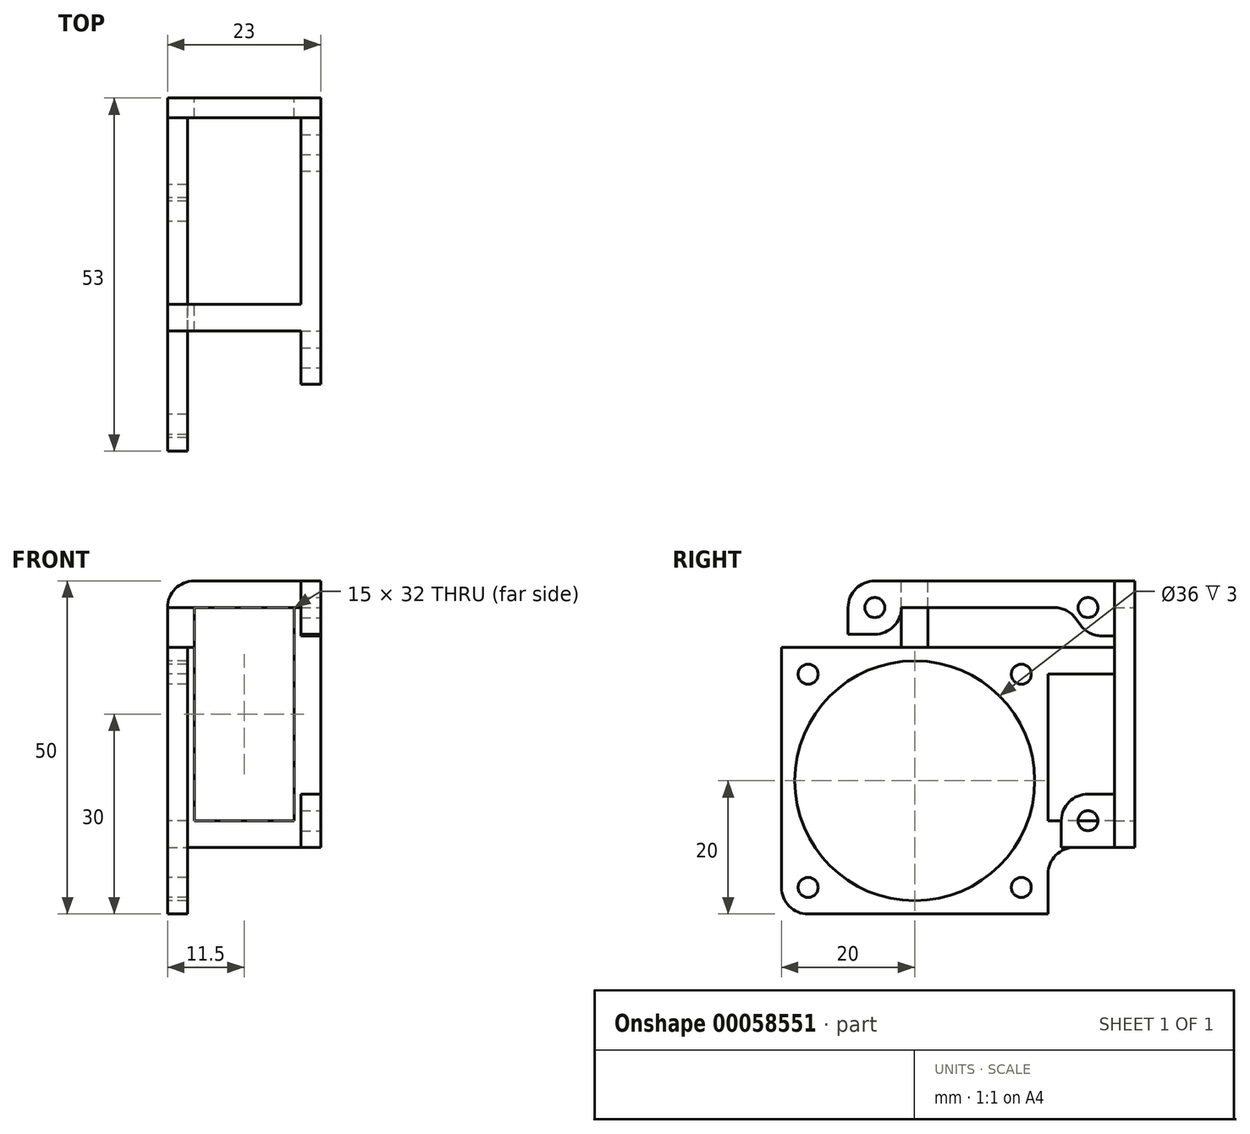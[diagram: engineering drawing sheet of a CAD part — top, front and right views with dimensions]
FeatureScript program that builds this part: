
annotation { "Feature Type Name" : "Feature", "Feature Type Description" : "" }
export const myFeature = defineFeature(function(context is Context, id is Id, definition is map)
    precondition{}
    {
        {
            var Q0;
            Q0=qCreatedBy(makeId("Top.planeOp"),FACE);
            var sketch = newSketch(context, id + "F0", { "sketchPlane" : qUnion([Q0])});
            skLineSegment(sketch, "E0.bottom", {"start": v(0, 0) * mm, "end": v(3, 0) * mm});
            skLineSegment(sketch, "E0.top", {"start": v(0, 40) * mm, "end": v(3, 40) * mm});
            skLineSegment(sketch, "E0.left", {"start": v(0, 0) * mm, "end": v(0, 40) * mm});
            skLineSegment(sketch, "E0.right", {"start": v(3, 0) * mm, "end": v(3, 40) * mm});
            skLineSegment(sketch, "E1.bottom", {"start": v(3, 40) * mm, "end": v(0, 40) * mm});
            skLineSegment(sketch, "E1.top", {"start": v(3, 50) * mm, "end": v(0, 50) * mm});
            skLineSegment(sketch, "E1.left", {"start": v(3, 40) * mm, "end": v(3, 50) * mm});
            skLineSegment(sketch, "E1.right", {"start": v(0, 40) * mm, "end": v(0, 50) * mm});
            skSolve(sketch);
        }
        {
            var Q0;
            Q0=qCreatedBy(makeId("Top.planeOp"),FACE);
            var sketch = newSketch(context, id + "F1", { "sketchPlane" : qUnion([Q0])});
            skLineSegment(sketch, "E2.bottom", {"start": v(0, 53) * mm, "end": v(23, 53) * mm});
            skLineSegment(sketch, "E2.top", {"start": v(0, 50) * mm, "end": v(23, 50) * mm});
            skLineSegment(sketch, "E2.left", {"start": v(0, 53) * mm, "end": v(0, 50) * mm});
            skLineSegment(sketch, "E2.right", {"start": v(23, 53) * mm, "end": v(23, 50) * mm});
            skSolve(sketch);
        }
        {
            var Q0;
            Q0=qCreatedBy(makeId("Top.planeOp"),FACE);
            var sketch = newSketch(context, id + "F2", { "sketchPlane" : qUnion([Q0])});
            skLineSegment(sketch, "E3.bottom", {"start": v(20, 50) * mm, "end": v(23, 50) * mm});
            skLineSegment(sketch, "E3.top", {"start": v(20, 10) * mm, "end": v(23, 10) * mm});
            skLineSegment(sketch, "E3.left", {"start": v(20, 50) * mm, "end": v(20, 10) * mm});
            skLineSegment(sketch, "E3.right", {"start": v(23, 50) * mm, "end": v(23, 10) * mm});
            skSolve(sketch);
        }
        {
            var Q0;
            Q0 = qSketchRegion(id + "F0", true);
            extrude(context, id + "F3", {"entities" : qUnion([Q0]), "oppositeDirection" : true, "depth" : (40 + 10) * mm});
        }
        {
            var Q0;
            Q0 = qSketchRegion(id + "F2", true);
            extrude(context, id + "F4", {"entities" : qUnion([Q0]), "oppositeDirection" : true, "depth" : 40 * mm});
        }
        {
            var Q0;
            Q0 = qSketchRegion(id + "F1", true);
            extrude(context, id + "F5", {"entities" : qUnion([Q0]), "oppositeDirection" : true, "depth" : 40 * mm});
        }
        {
            var Q0;
            Q0=makeQuery(id+"F3.opExtrude","SWEPT_FACE",FACE,{"disambiguationData":[OSD([sQuery(id+"F0.wireOp",EDGE,"E0.left"),sQuery(id+"F0.wireOp",EDGE,"E1.right")])]});
            var sketch = newSketch(context, id + "F6", { "sketchPlane" : qUnion([Q0])});
            skCircle(sketch, "E4", {"center": v(-20, -30) * mm, "radius": 18 * mm});
            skSolve(sketch);
        }
        {
            var Q0;
            Q0 = qSketchRegion(id + "F6", true);
            extrude(context, id + "F7", {"entities" : qUnion([Q0]), "operationType" : NewBodyOperationType.REMOVE, "oppositeDirection" : true, "depth" : 3 * mm});
        }
        {
            var Q0;
            Q0=makeQuery(id+"F3.opExtrude","SWEPT_FACE",FACE,{"disambiguationData":[OSD([sQuery(id+"F0.wireOp",EDGE,"E0.left"),sQuery(id+"F0.wireOp",EDGE,"E1.right")])]});
            var sketch = newSketch(context, id + "F8", { "sketchPlane" : qUnion([Q0])});
            skCircle(sketch, "E5", {"center": v(-4, -14) * mm, "radius": 1.5 * mm});
            skCircle(sketch, "E6", {"center": v(-4, -46) * mm, "radius": 1.5 * mm});
            skCircle(sketch, "E7", {"center": v(-36, -14) * mm, "radius": 1.5 * mm});
            skCircle(sketch, "E8", {"center": v(-36, -46) * mm, "radius": 1.5 * mm});
            skSolve(sketch);
        }
        {
            var Q0;
            Q0 = qSketchRegion(id + "F8", true);
            extrude(context, id + "F9", {"entities" : qUnion([Q0]), "operationType" : NewBodyOperationType.REMOVE, "oppositeDirection" : true, "depth" : 3 * mm});
        }
        {
            var Q0;
            Q0=makeQuery(id+"F4.opExtrude","SWEPT_FACE",FACE,{"disambiguationData":[OSD([sQuery(id+"F2.wireOp",EDGE,"E3.right")])]});
            var sketch = newSketch(context, id + "F10", { "sketchPlane" : qUnion([Q0])});
            skLineSegment(sketch, "E9", {"start": v(10, -8) * mm, "end": v(18, -8) * mm});
            skLineSegment(sketch, "E10", {"start": v(18, -8) * mm, "end": v(18, -4) * mm});
            skLineSegment(sketch, "E11", {"start": v(18, -4) * mm, "end": v(43.01, -4) * mm});
            skLineSegment(sketch, "E12", {"start": v(43.01, -4) * mm, "end": v(46, -8.25) * mm});
            skLineSegment(sketch, "E13", {"start": v(46, -8.25) * mm, "end": v(46, -32) * mm});
            skLineSegment(sketch, "E14", {"start": v(46, -32) * mm, "end": v(42, -32) * mm});
            skLineSegment(sketch, "E15", {"start": v(42, -32) * mm, "end": v(42, -40) * mm});
            skLineSegment(sketch, "E16", {"start": v(42, -40) * mm, "end": v(50, -40) * mm});
            skLineSegment(sketch, "E17", {"start": v(50, -40) * mm, "end": v(50, 0) * mm});
            skLineSegment(sketch, "E18", {"start": v(50, 0) * mm, "end": v(10, 0) * mm});
            skLineSegment(sketch, "E19", {"start": v(10, 0) * mm, "end": v(10, -8) * mm});
            skSolve(sketch);
        }
        {
            var Q0;
            {var subQ5=sQuery(id+"F10.wireOp",EDGE,"E9");Q0=makeQuery(id+"F10.imprint","IMPRINT",FACE,{"disambiguationData":[TD([[makeQuery(id+"F10.imprint","IMPRINT",EDGE,{"derivedFrom":subQ5}),-1.0]])]});}
            extrude(context, id + "F11", {"entities" : qUnion([Q0]), "operationType" : NewBodyOperationType.REMOVE, "oppositeDirection" : true, "depth" : 3 * mm});
        }
        {
            var Q0;
            Q0=makeQuery(id+"F4.opExtrude","SWEPT_FACE",FACE,{"disambiguationData":[OSD([sQuery(id+"F2.wireOp",EDGE,"E3.right")])]});
            var sketch = newSketch(context, id + "F12", { "sketchPlane" : qUnion([Q0])});
            skCircle(sketch, "E20", {"center": v(14, -4) * mm, "radius": 1.5 * mm});
            skCircle(sketch, "E21", {"center": v(46, -4) * mm, "radius": 1.5 * mm});
            skCircle(sketch, "E22", {"center": v(46, -36) * mm, "radius": 1.5 * mm});
            skSolve(sketch);
        }
        {
            var Q0;
            Q0 = qSketchRegion(id + "F12", true);
            extrude(context, id + "F13", {"entities" : qUnion([Q0]), "operationType" : NewBodyOperationType.REMOVE, "oppositeDirection" : true, "depth" : 3 * mm});
        }
        {
            var Q0;
            Q0=makeQuery(id+"F5.opExtrude","SWEPT_FACE",FACE,{"disambiguationData":[OSD([sQuery(id+"F1.wireOp",EDGE,"E2.bottom")])]});
            var sketch = newSketch(context, id + "F14", { "sketchPlane" : qUnion([Q0])});
            skLineSegment(sketch, "E23.bottom", {"start": v(-19, -4) * mm, "end": v(-4, -4) * mm});
            skLineSegment(sketch, "E23.top", {"start": v(-19, -36) * mm, "end": v(-4, -36) * mm});
            skLineSegment(sketch, "E23.left", {"start": v(-19, -4) * mm, "end": v(-19, -36) * mm});
            skLineSegment(sketch, "E23.right", {"start": v(-4, -4) * mm, "end": v(-4, -36) * mm});
            skSolve(sketch);
        }
        {
            var Q0;
            Q0 = qSketchRegion(id + "F14", true);
            extrude(context, id + "F15", {"entities" : qUnion([Q0]), "operationType" : NewBodyOperationType.REMOVE, "oppositeDirection" : true, "depth" : 3 * mm});
        }
        {
            var Q0;
            Q0=makeQuery(id+"F3.opExtrude","SWEPT_FACE",FACE,{"disambiguationData":[OSD([sQuery(id+"F0.wireOp",EDGE,"E0.left"),sQuery(id+"F0.wireOp",EDGE,"E1.right")])]});
            var sketch = newSketch(context, id + "F16", { "sketchPlane" : qUnion([Q0])});
            skLineSegment(sketch, "E24.bottom", {"start": v(-50, -50) * mm, "end": v(-40, -50) * mm});
            skLineSegment(sketch, "E24.top", {"start": v(-50, -40) * mm, "end": v(-40, -40) * mm});
            skLineSegment(sketch, "E24.left", {"start": v(-50, -50) * mm, "end": v(-50, -40) * mm});
            skLineSegment(sketch, "E24.right", {"start": v(-40, -50) * mm, "end": v(-40, -40) * mm});
            skSolve(sketch);
        }
        {
            var Q0;
            Q0 = qSketchRegion(id + "F16", true);
            extrude(context, id + "F17", {"entities" : qUnion([Q0]), "operationType" : NewBodyOperationType.REMOVE, "oppositeDirection" : true, "depth" : 3 * mm});
        }
        {
            var Q0;
            Q0=makeQuery(id+"F3.opExtrude","SWEPT_FACE",FACE,{"disambiguationData":[OSD([sQuery(id+"F0.wireOp",EDGE,"E0.left"),sQuery(id+"F0.wireOp",EDGE,"E1.right")])]});
            var sketch = newSketch(context, id + "F18", { "sketchPlane" : qUnion([Q0])});
            skLineSegment(sketch, "E25.bottom", {"start": v(-50, -36) * mm, "end": v(-40, -36) * mm});
            skLineSegment(sketch, "E25.top", {"start": v(-50, -14) * mm, "end": v(-40, -14) * mm});
            skLineSegment(sketch, "E25.left", {"start": v(-50, -36) * mm, "end": v(-50, -14) * mm});
            skLineSegment(sketch, "E25.right", {"start": v(-40, -36) * mm, "end": v(-40, -14) * mm});
            skLineSegment(sketch, "E26.bottom", {"start": v(-50, 0) * mm, "end": v(0, 0) * mm});
            skLineSegment(sketch, "E26.top", {"start": v(-50, -10) * mm, "end": v(0, -10) * mm});
            skLineSegment(sketch, "E26.left", {"start": v(-50, 0) * mm, "end": v(-50, -10) * mm});
            skLineSegment(sketch, "E26.right", {"start": v(0, 0) * mm, "end": v(0, -10) * mm});
            skSolve(sketch);
        }
        {
            var Q0;
            Q0 = qSketchRegion(id + "F18", true);
            extrude(context, id + "F19", {"entities" : qUnion([Q0]), "operationType" : NewBodyOperationType.REMOVE, "oppositeDirection" : true, "depth" : 3 * mm});
        }
        {
            var Q0;
            Q0=makeQuery(id+"F4.opExtrude","SWEPT_FACE",FACE,{"disambiguationData":[OSD([sQuery(id+"F2.wireOp",EDGE,"E3.right")])]});
            var sketch = newSketch(context, id + "F20", { "sketchPlane" : qUnion([Q0])});
            skLineSegment(sketch, "E27.bottom", {"start": v(46, -8.25) * mm, "end": v(50, -8.25) * mm});
            skLineSegment(sketch, "E27.top", {"start": v(46, -32) * mm, "end": v(50, -32) * mm});
            skLineSegment(sketch, "E27.left", {"start": v(46, -8.25) * mm, "end": v(46, -32) * mm});
            skLineSegment(sketch, "E27.right", {"start": v(50, -8.25) * mm, "end": v(50, -32) * mm});
            skSolve(sketch);
        }
        {
            var Q0;
            Q0 = qSketchRegion(id + "F20", true);
            extrude(context, id + "F21", {"entities" : qUnion([Q0]), "operationType" : NewBodyOperationType.REMOVE, "oppositeDirection" : true, "depth" : 3 * mm});
        }
        {
            var Q0;
            Q0=makeQuery(id+"F4.opExtrude","CAP_EDGE",EDGE,{"disambiguationData":[OSD([sQuery(id+"F2.wireOp",EDGE,"E3.top")])],"isStart":true});
            var Q1;
            Q1=makeQuery(id+"F19.boolean.opBoolean","COPY",EDGE,{"derivedFrom":makeQuery(id+"F19.opExtrude","SWEPT_EDGE",EDGE,{"disambiguationData":[OSD([sQuery(id+"F0.wireOp",EDGE,"E0.bottom"),sQuery(id+"F0.wireOp",EDGE,"E0.left"),sQuery(id+"F18.wireOp",EDGE,"E26.top"),sQuery(id+"F18.wireOp",EDGE,"E26.right")])]})});
            var Q2;
            Q2=makeQuery(id+"F11.boolean.opBoolean","COPY",EDGE,{"derivedFrom":makeQuery(id+"F11.opExtrude","SWEPT_EDGE",EDGE,{"disambiguationData":[OSD([sQuery(id+"F2.wireOp",EDGE,"E3.top"),sQuery(id+"F2.wireOp",EDGE,"E3.right"),sQuery(id+"F10.wireOp",EDGE,"E9"),sQuery(id+"F10.wireOp",EDGE,"E19")])]})});
            var Q3;
            Q3=makeQuery(id+"F11.boolean.opBoolean","COPY",EDGE,{"derivedFrom":makeQuery(id+"F11.opExtrude","SWEPT_EDGE",EDGE,{"disambiguationData":[OSD([sQuery(id+"F10.wireOp",EDGE,"E9"),sQuery(id+"F10.wireOp",EDGE,"E10")])]})});
            var Q4;
            Q4=makeQuery(id+"F11.boolean.opBoolean","COPY",EDGE,{"derivedFrom":makeQuery(id+"F11.opExtrude","SWEPT_EDGE",EDGE,{"disambiguationData":[OSD([sQuery(id+"F10.wireOp",EDGE,"E11"),sQuery(id+"F10.wireOp",EDGE,"E12")])]})});
            var Q5;
            Q5=makeQuery(id+"F3.opExtrude","CAP_EDGE",EDGE,{"disambiguationData":[OSD([sQuery(id+"F0.wireOp",EDGE,"E0.bottom")])],"isStart":false});
            var Q6;
            Q6=makeQuery(id+"F17.boolean.opBoolean","COPY",EDGE,{"derivedFrom":makeQuery(id+"F17.opExtrude","SWEPT_EDGE",EDGE,{"disambiguationData":[OSD([sQuery(id+"F0.wireOp",EDGE,"E0.left"),sQuery(id+"F0.wireOp",EDGE,"E1.right"),sQuery(id+"F16.wireOp",EDGE,"E24.bottom"),sQuery(id+"F16.wireOp",EDGE,"E24.right")])]})});
            var Q7;
            Q7=makeQuery(id+"F17.boolean.opBoolean","COPY",EDGE,{"derivedFrom":makeQuery(id+"F17.opExtrude","SWEPT_EDGE",EDGE,{"disambiguationData":[OSD([sQuery(id+"F16.wireOp",EDGE,"E24.top"),sQuery(id+"F16.wireOp",EDGE,"E24.right")])]})});
            var Q8;
            Q8=makeQuery(id+"F11.boolean.opBoolean","COPY",EDGE,{"derivedFrom":makeQuery(id+"F11.opExtrude","SWEPT_EDGE",EDGE,{"disambiguationData":[OSD([sQuery(id+"F2.wireOp",EDGE,"E3.right"),sQuery(id+"F10.wireOp",EDGE,"E15"),sQuery(id+"F10.wireOp",EDGE,"E16")])]})});
            var Q9;
            Q9=makeQuery(id+"F11.boolean.opBoolean","COPY",EDGE,{"derivedFrom":makeQuery(id+"F11.opExtrude","SWEPT_EDGE",EDGE,{"disambiguationData":[OSD([sQuery(id+"F10.wireOp",EDGE,"E14"),sQuery(id+"F10.wireOp",EDGE,"E15")])]})});
            var Q10;
            {var subQ0=sQuery(id+"F10.wireOp",EDGE,"E12");Q10=makeQuery(id+"F21.boolean.opBoolean","MERGE",EDGE,{"derivedFrom":[makeQuery(id+"F11.boolean.opBoolean","COPY",EDGE,{"derivedFrom":makeQuery(id+"F11.opExtrude","SWEPT_EDGE",EDGE,{"disambiguationData":[OSD([subQ0,sQuery(id+"F10.wireOp",EDGE,"E13")])]})}),makeQuery(id+"F21.opExtrude","SWEPT_EDGE",EDGE,{"disambiguationData":[OSD([subQ0,sQuery(id+"F20.wireOp",EDGE,"E27.bottom"),sQuery(id+"F20.wireOp",EDGE,"E27.left")])]})]});}
            fillet(context, id + "F22", {"entities" : qUnion([Q0, Q1, Q2, Q3, Q4, Q5, Q6, Q7, Q8, Q9, Q10]), "radius" : 4 * mm, "tangentPropagation" : true, "allowEdgeOverflow" : false});
        }
        {
            var Q0;
            {var subQ0=sQuery(id+"F2.wireOp",EDGE,"E3.top");var subQ1=sQuery(id+"F2.wireOp",EDGE,"E3.left");Q0=makeQuery(id+"F21.boolean.opBoolean","SPLIT",FACE,{"disambiguationData":[TD([makeQuery(id+"F4.opExtrude","SWEPT_FACE",FACE,{"disambiguationData":[OSD([subQ0])]})])],"derivedFrom":makeQuery(id+"F4.opExtrude","SWEPT_FACE",FACE,{"disambiguationData":[OSD([subQ1])]})});}
            var sketch = newSketch(context, id + "F23", { "sketchPlane" : qUnion([Q0])});
            skLineSegment(sketch, "E28.bottom", {"start": v(-18, -4) * mm, "end": v(-22, -4) * mm});
            skLineSegment(sketch, "E28.top", {"start": v(-18, 0) * mm, "end": v(-22, 0) * mm});
            skLineSegment(sketch, "E28.left", {"start": v(-18, -4) * mm, "end": v(-18, 0) * mm});
            skLineSegment(sketch, "E28.right", {"start": v(-22, -4) * mm, "end": v(-22, 0) * mm});
            skSolve(sketch);
        }
        {
            var Q0;
            Q0 = qSketchRegion(id + "F23", true);
            extrude(context, id + "F24", {"entities" : qUnion([Q0]), "operationType" : NewBodyOperationType.ADD, "depth" : 20 * mm});
        }
        {
            var Q0;
            Q0=makeQuery(id+"F24.boolean.opBoolean","MERGE",FACE,{"derivedFrom":[makeQuery(id+"F11.boolean.opBoolean","COPY",FACE,{"derivedFrom":makeQuery(id+"F11.opExtrude","SWEPT_FACE",FACE,{"disambiguationData":[OSD([sQuery(id+"F10.wireOp",EDGE,"E11")])]})}),makeQuery(id+"F24.opExtrude","SWEPT_FACE",FACE,{"disambiguationData":[OSD([sQuery(id+"F23.wireOp",EDGE,"E28.bottom")])]})]});
            var sketch = newSketch(context, id + "F25", { "sketchPlane" : qUnion([Q0])});
            skLineSegment(sketch, "E29.bottom", {"start": v(0, -18) * mm, "end": v(4, -18) * mm});
            skLineSegment(sketch, "E29.top", {"start": v(0, -22) * mm, "end": v(4, -22) * mm});
            skLineSegment(sketch, "E29.left", {"start": v(0, -18) * mm, "end": v(0, -22) * mm});
            skLineSegment(sketch, "E29.right", {"start": v(4, -18) * mm, "end": v(4, -22) * mm});
            skSolve(sketch);
        }
        {
            var Q0;
            Q0 = qSketchRegion(id + "F25", true);
            var Q1;
            Q1=makeQuery(id+"F19.boolean.opBoolean","COPY",FACE,{"derivedFrom":makeQuery(id+"F19.opExtrude","SWEPT_FACE",FACE,{"disambiguationData":[OSD([sQuery(id+"F18.wireOp",EDGE,"E26.top")])]})});
            extrude(context, id + "F26", {"entities" : qUnion([Q0]), "endBound" : BoundingType.UP_TO_SURFACE, "endBoundEntityFace" : qUnion([Q1]), "depth" : 25 * mm});
        }
        {
            var Q0;
            Q0=makeQuery(id+"F5.opExtrude","CAP_EDGE",EDGE,{"disambiguationData":[OSD([sQuery(id+"F1.wireOp",EDGE,"E2.left")])],"isStart":true});
            var Q1;
            Q1=makeQuery(id+"F24.opExtrude","CAP_EDGE",EDGE,{"disambiguationData":[OSD([sQuery(id+"F23.wireOp",EDGE,"E28.top")])],"isStart":false});
            fillet(context, id + "F27", {"entities" : qUnion([Q0, Q1]), "radius" : 4 * mm, "tangentPropagation" : true, "allowEdgeOverflow" : false});
        }
    });
